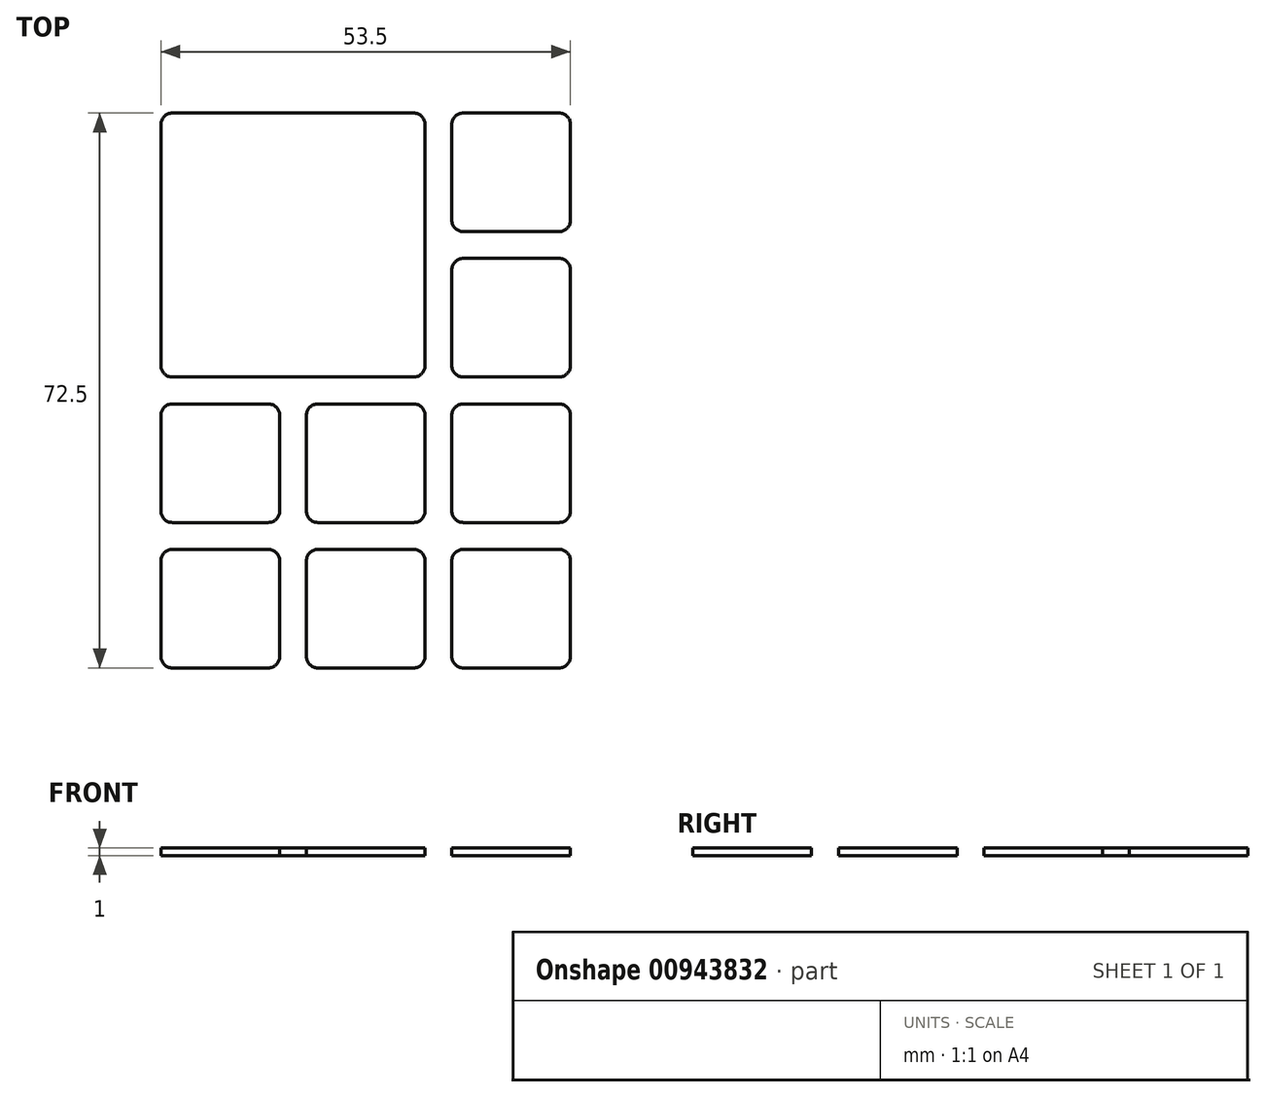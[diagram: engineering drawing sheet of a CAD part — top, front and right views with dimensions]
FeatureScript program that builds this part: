
annotation { "Feature Type Name" : "Feature", "Feature Type Description" : "" }
export const myFeature = defineFeature(function(context is Context, id is Id, definition is map)
    precondition{}
    {
        {
            var Q0;
            Q0=qCreatedBy(makeId("Top.planeOp"),FACE);
            var sketch = newSketch(context, id + "F0", { "sketchPlane" : qUnion([Q0])});
            skLineSegment(sketch, "E0.bottom", {"start": v(0, 0) * mm, "end": v(19, 0) * mm, "construction": true});
            skLineSegment(sketch, "E0.top", {"start": v(0, 19) * mm, "end": v(19, 19) * mm, "construction": true});
            skLineSegment(sketch, "E0.left", {"start": v(0, 0) * mm, "end": v(0, 19) * mm, "construction": true});
            skLineSegment(sketch, "E0.right", {"start": v(19, 0) * mm, "end": v(19, 19) * mm, "construction": true});
            skLineSegment(sketch, "E1.bottom", {"start": v(3.25, 17.25) * mm, "end": v(15.75, 17.25) * mm});
            skLineSegment(sketch, "E1.top", {"start": v(3.25, 1.75) * mm, "end": v(15.75, 1.75) * mm});
            skLineSegment(sketch, "E1.left", {"start": v(1.75, 15.75) * mm, "end": v(1.75, 3.25) * mm});
            skLineSegment(sketch, "E1.right", {"start": v(17.25, 15.75) * mm, "end": v(17.25, 3.25) * mm});
            skPoint(sketch, "E2.visualSharp", {"position": v(1.75, 17.25) * mm});
            skArc(sketch, "E2.filletArc", {"start": v(3.25, 17.25) * mm, "mid": v(2.19, 16.81) * mm, "end": v(1.75, 15.75) * mm});
            skPoint(sketch, "E3.visualSharp", {"position": v(17.25, 17.25) * mm});
            skArc(sketch, "E3.filletArc", {"start": v(17.25, 15.75) * mm, "mid": v(16.81, 16.81) * mm, "end": v(15.75, 17.25) * mm});
            skPoint(sketch, "E4.visualSharp", {"position": v(17.25, 1.75) * mm});
            skArc(sketch, "E4.filletArc", {"start": v(15.75, 1.75) * mm, "mid": v(16.81, 2.19) * mm, "end": v(17.25, 3.25) * mm});
            skPoint(sketch, "E5.visualSharp", {"position": v(1.75, 1.75) * mm});
            skArc(sketch, "E5.filletArc", {"start": v(1.75, 3.25) * mm, "mid": v(2.19, 2.19) * mm, "end": v(3.25, 1.75) * mm});
            skArc(sketch, "E6.0.1.0", {"start": v(17.25, 34.75) * mm, "mid": v(16.81, 35.81) * mm, "end": v(15.75, 36.25) * mm});
            skPoint(sketch, "E6.0.1.1", {"position": v(17.25, 36.25) * mm});
            skArc(sketch, "E6.0.1.2", {"start": v(15.75, 20.75) * mm, "mid": v(16.81, 21.19) * mm, "end": v(17.25, 22.25) * mm});
            skLineSegment(sketch, "E6.0.1.3", {"start": v(3.25, 36.25) * mm, "end": v(15.75, 36.25) * mm});
            skLineSegment(sketch, "E6.0.1.4", {"start": v(17.25, 34.75) * mm, "end": v(17.25, 22.25) * mm});
            skPoint(sketch, "E6.0.1.5", {"position": v(1.75, 20.75) * mm});
            skArc(sketch, "E6.0.1.6", {"start": v(3.25, 36.25) * mm, "mid": v(2.19, 35.81) * mm, "end": v(1.75, 34.75) * mm});
            skPoint(sketch, "E6.0.1.7", {"position": v(17.25, 20.75) * mm});
            skArc(sketch, "E6.0.1.8", {"start": v(1.75, 22.25) * mm, "mid": v(2.19, 21.19) * mm, "end": v(3.25, 20.75) * mm});
            skLineSegment(sketch, "E6.0.1.9", {"start": v(1.75, 34.75) * mm, "end": v(1.75, 22.25) * mm});
            skLineSegment(sketch, "E6.0.1.10", {"start": v(3.25, 20.75) * mm, "end": v(15.75, 20.75) * mm});
            skPoint(sketch, "E6.0.1.11", {"position": v(1.75, 36.25) * mm});
            skPoint(sketch, "E6.0.2.5", {"position": v(1.75, 39.75) * mm});
            skArc(sketch, "E6.0.2.8", {"start": v(1.75, 41.25) * mm, "mid": v(2.19, 40.19) * mm, "end": v(3.25, 39.75) * mm});
            skLineSegment(sketch, "E6.0.2.9", {"start": v(1.75, 53.75) * mm, "end": v(1.75, 41.25) * mm});
            skLineSegment(sketch, "E6.0.2.10", {"start": v(3.25, 39.75) * mm, "end": v(15.75, 39.75) * mm});
            skPoint(sketch, "E6.0.2.11", {"position": v(1.75, 55.25) * mm});
            skLineSegment(sketch, "E6.0.3.3", {"start": v(3.25, 74.25) * mm, "end": v(15.75, 74.25) * mm});
            skPoint(sketch, "E6.0.3.5", {"position": v(1.75, 58.75) * mm});
            skArc(sketch, "E6.0.3.6", {"start": v(3.25, 74.25) * mm, "mid": v(2.19, 73.81) * mm, "end": v(1.75, 72.75) * mm});
            skLineSegment(sketch, "E6.0.3.9", {"start": v(1.75, 72.75) * mm, "end": v(1.75, 60.25) * mm});
            skPoint(sketch, "E6.0.3.11", {"position": v(1.75, 74.25) * mm});
            skArc(sketch, "E6.1.0.0", {"start": v(36.25, 15.75) * mm, "mid": v(35.81, 16.81) * mm, "end": v(34.75, 17.25) * mm});
            skPoint(sketch, "E6.1.0.1", {"position": v(36.25, 17.25) * mm});
            skArc(sketch, "E6.1.0.2", {"start": v(34.75, 1.75) * mm, "mid": v(35.81, 2.19) * mm, "end": v(36.25, 3.25) * mm});
            skLineSegment(sketch, "E6.1.0.3", {"start": v(22.25, 17.25) * mm, "end": v(34.75, 17.25) * mm});
            skLineSegment(sketch, "E6.1.0.4", {"start": v(36.25, 15.75) * mm, "end": v(36.25, 3.25) * mm});
            skPoint(sketch, "E6.1.0.5", {"position": v(20.75, 1.75) * mm});
            skArc(sketch, "E6.1.0.6", {"start": v(22.25, 17.25) * mm, "mid": v(21.19, 16.81) * mm, "end": v(20.75, 15.75) * mm});
            skPoint(sketch, "E6.1.0.7", {"position": v(36.25, 1.75) * mm});
            skArc(sketch, "E6.1.0.8", {"start": v(20.75, 3.25) * mm, "mid": v(21.19, 2.19) * mm, "end": v(22.25, 1.75) * mm});
            skLineSegment(sketch, "E6.1.0.9", {"start": v(20.75, 15.75) * mm, "end": v(20.75, 3.25) * mm});
            skLineSegment(sketch, "E6.1.0.10", {"start": v(22.25, 1.75) * mm, "end": v(34.75, 1.75) * mm});
            skPoint(sketch, "E6.1.0.11", {"position": v(20.75, 17.25) * mm});
            skArc(sketch, "E6.1.1.0", {"start": v(36.25, 34.75) * mm, "mid": v(35.81, 35.81) * mm, "end": v(34.75, 36.25) * mm});
            skPoint(sketch, "E6.1.1.1", {"position": v(36.25, 36.25) * mm});
            skArc(sketch, "E6.1.1.2", {"start": v(34.75, 20.75) * mm, "mid": v(35.81, 21.19) * mm, "end": v(36.25, 22.25) * mm});
            skLineSegment(sketch, "E6.1.1.3", {"start": v(22.25, 36.25) * mm, "end": v(34.75, 36.25) * mm});
            skLineSegment(sketch, "E6.1.1.4", {"start": v(36.25, 34.75) * mm, "end": v(36.25, 22.25) * mm});
            skPoint(sketch, "E6.1.1.5", {"position": v(20.75, 20.75) * mm});
            skArc(sketch, "E6.1.1.6", {"start": v(22.25, 36.25) * mm, "mid": v(21.19, 35.81) * mm, "end": v(20.75, 34.75) * mm});
            skPoint(sketch, "E6.1.1.7", {"position": v(36.25, 20.75) * mm});
            skArc(sketch, "E6.1.1.8", {"start": v(20.75, 22.25) * mm, "mid": v(21.19, 21.19) * mm, "end": v(22.25, 20.75) * mm});
            skLineSegment(sketch, "E6.1.1.9", {"start": v(20.75, 34.75) * mm, "end": v(20.75, 22.25) * mm});
            skLineSegment(sketch, "E6.1.1.10", {"start": v(22.25, 20.75) * mm, "end": v(34.75, 20.75) * mm});
            skPoint(sketch, "E6.1.1.11", {"position": v(20.75, 36.25) * mm});
            skArc(sketch, "E6.1.2.2", {"start": v(34.75, 39.75) * mm, "mid": v(35.81, 40.19) * mm, "end": v(36.25, 41.25) * mm});
            skLineSegment(sketch, "E6.1.2.4", {"start": v(36.25, 53.75) * mm, "end": v(36.25, 41.25) * mm});
            skPoint(sketch, "E6.1.2.7", {"position": v(36.25, 39.75) * mm});
            skLineSegment(sketch, "E6.1.2.10", {"start": v(22.25, 39.75) * mm, "end": v(34.75, 39.75) * mm});
            skArc(sketch, "E6.1.3.0", {"start": v(36.25, 72.75) * mm, "mid": v(35.81, 73.81) * mm, "end": v(34.75, 74.25) * mm});
            skPoint(sketch, "E6.1.3.1", {"position": v(36.25, 74.25) * mm});
            skLineSegment(sketch, "E6.1.3.3", {"start": v(22.25, 74.25) * mm, "end": v(34.75, 74.25) * mm});
            skLineSegment(sketch, "E6.1.3.4", {"start": v(36.25, 72.75) * mm, "end": v(36.25, 60.25) * mm});
            skArc(sketch, "E6.2.0.0", {"start": v(55.25, 15.75) * mm, "mid": v(54.81, 16.81) * mm, "end": v(53.75, 17.25) * mm});
            skPoint(sketch, "E6.2.0.1", {"position": v(55.25, 17.25) * mm});
            skArc(sketch, "E6.2.0.2", {"start": v(53.75, 1.75) * mm, "mid": v(54.81, 2.19) * mm, "end": v(55.25, 3.25) * mm});
            skLineSegment(sketch, "E6.2.0.3", {"start": v(41.25, 17.25) * mm, "end": v(53.75, 17.25) * mm});
            skLineSegment(sketch, "E6.2.0.4", {"start": v(55.25, 15.75) * mm, "end": v(55.25, 3.25) * mm});
            skPoint(sketch, "E6.2.0.5", {"position": v(39.75, 1.75) * mm});
            skArc(sketch, "E6.2.0.6", {"start": v(41.25, 17.25) * mm, "mid": v(40.19, 16.81) * mm, "end": v(39.75, 15.75) * mm});
            skPoint(sketch, "E6.2.0.7", {"position": v(55.25, 1.75) * mm});
            skArc(sketch, "E6.2.0.8", {"start": v(39.75, 3.25) * mm, "mid": v(40.19, 2.19) * mm, "end": v(41.25, 1.75) * mm});
            skLineSegment(sketch, "E6.2.0.9", {"start": v(39.75, 15.75) * mm, "end": v(39.75, 3.25) * mm});
            skLineSegment(sketch, "E6.2.0.10", {"start": v(41.25, 1.75) * mm, "end": v(53.75, 1.75) * mm});
            skPoint(sketch, "E6.2.0.11", {"position": v(39.75, 17.25) * mm});
            skArc(sketch, "E6.2.1.0", {"start": v(55.25, 34.75) * mm, "mid": v(54.81, 35.81) * mm, "end": v(53.75, 36.25) * mm});
            skPoint(sketch, "E6.2.1.1", {"position": v(55.25, 36.25) * mm});
            skArc(sketch, "E6.2.1.2", {"start": v(53.75, 20.75) * mm, "mid": v(54.81, 21.19) * mm, "end": v(55.25, 22.25) * mm});
            skLineSegment(sketch, "E6.2.1.3", {"start": v(41.25, 36.25) * mm, "end": v(53.75, 36.25) * mm});
            skLineSegment(sketch, "E6.2.1.4", {"start": v(55.25, 34.75) * mm, "end": v(55.25, 22.25) * mm});
            skPoint(sketch, "E6.2.1.5", {"position": v(39.75, 20.75) * mm});
            skArc(sketch, "E6.2.1.6", {"start": v(41.25, 36.25) * mm, "mid": v(40.19, 35.81) * mm, "end": v(39.75, 34.75) * mm});
            skPoint(sketch, "E6.2.1.7", {"position": v(55.25, 20.75) * mm});
            skArc(sketch, "E6.2.1.8", {"start": v(39.75, 22.25) * mm, "mid": v(40.19, 21.19) * mm, "end": v(41.25, 20.75) * mm});
            skLineSegment(sketch, "E6.2.1.9", {"start": v(39.75, 34.75) * mm, "end": v(39.75, 22.25) * mm});
            skLineSegment(sketch, "E6.2.1.10", {"start": v(41.25, 20.75) * mm, "end": v(53.75, 20.75) * mm});
            skPoint(sketch, "E6.2.1.11", {"position": v(39.75, 36.25) * mm});
            skArc(sketch, "E6.2.2.0", {"start": v(55.25, 53.75) * mm, "mid": v(54.81, 54.81) * mm, "end": v(53.75, 55.25) * mm});
            skPoint(sketch, "E6.2.2.1", {"position": v(55.25, 55.25) * mm});
            skArc(sketch, "E6.2.2.2", {"start": v(53.75, 39.75) * mm, "mid": v(54.81, 40.19) * mm, "end": v(55.25, 41.25) * mm});
            skLineSegment(sketch, "E6.2.2.3", {"start": v(41.25, 55.25) * mm, "end": v(53.75, 55.25) * mm});
            skLineSegment(sketch, "E6.2.2.4", {"start": v(55.25, 53.75) * mm, "end": v(55.25, 41.25) * mm});
            skPoint(sketch, "E6.2.2.5", {"position": v(39.75, 39.75) * mm});
            skArc(sketch, "E6.2.2.6", {"start": v(41.25, 55.25) * mm, "mid": v(40.19, 54.81) * mm, "end": v(39.75, 53.75) * mm});
            skPoint(sketch, "E6.2.2.7", {"position": v(55.25, 39.75) * mm});
            skArc(sketch, "E6.2.2.8", {"start": v(39.75, 41.25) * mm, "mid": v(40.19, 40.19) * mm, "end": v(41.25, 39.75) * mm});
            skLineSegment(sketch, "E6.2.2.9", {"start": v(39.75, 53.75) * mm, "end": v(39.75, 41.25) * mm});
            skLineSegment(sketch, "E6.2.2.10", {"start": v(41.25, 39.75) * mm, "end": v(53.75, 39.75) * mm});
            skPoint(sketch, "E6.2.2.11", {"position": v(39.75, 55.25) * mm});
            skArc(sketch, "E6.2.3.0", {"start": v(55.25, 72.75) * mm, "mid": v(54.81, 73.81) * mm, "end": v(53.75, 74.25) * mm});
            skPoint(sketch, "E6.2.3.1", {"position": v(55.25, 74.25) * mm});
            skArc(sketch, "E6.2.3.2", {"start": v(53.75, 58.75) * mm, "mid": v(54.81, 59.19) * mm, "end": v(55.25, 60.25) * mm});
            skLineSegment(sketch, "E6.2.3.3", {"start": v(41.25, 74.25) * mm, "end": v(53.75, 74.25) * mm});
            skLineSegment(sketch, "E6.2.3.4", {"start": v(55.25, 72.75) * mm, "end": v(55.25, 60.25) * mm});
            skPoint(sketch, "E6.2.3.5", {"position": v(39.75, 58.75) * mm});
            skArc(sketch, "E6.2.3.6", {"start": v(41.25, 74.25) * mm, "mid": v(40.19, 73.81) * mm, "end": v(39.75, 72.75) * mm});
            skPoint(sketch, "E6.2.3.7", {"position": v(55.25, 58.75) * mm});
            skArc(sketch, "E6.2.3.8", {"start": v(39.75, 60.25) * mm, "mid": v(40.19, 59.19) * mm, "end": v(41.25, 58.75) * mm});
            skLineSegment(sketch, "E6.2.3.9", {"start": v(39.75, 72.75) * mm, "end": v(39.75, 60.25) * mm});
            skLineSegment(sketch, "E6.2.3.10", {"start": v(41.25, 58.75) * mm, "end": v(53.75, 58.75) * mm});
            skPoint(sketch, "E6.2.3.11", {"position": v(39.75, 74.25) * mm});
            skLineSegment(sketch, "E6.direction1", {"start": v(1.75, 1.75) * mm, "end": v(20.75, 1.75) * mm, "construction": true});
            skLineSegment(sketch, "E6.direction2", {"start": v(1.75, 1.75) * mm, "end": v(1.75, 20.75) * mm, "construction": true});
            skLineSegment(sketch, "E7", {"start": v(1.75, 53.75) * mm, "end": v(1.75, 60.25) * mm});
            skLineSegment(sketch, "E8", {"start": v(36.25, 53.75) * mm, "end": v(36.25, 60.25) * mm});
            skLineSegment(sketch, "E9", {"start": v(15.75, 74.25) * mm, "end": v(22.25, 74.25) * mm});
            skLineSegment(sketch, "E10", {"start": v(15.75, 39.75) * mm, "end": v(22.25, 39.75) * mm});
            skSolve(sketch);
        }
        {
            var Q0;
            Q0=qSketchRegion(id+"F0",true);
            extrude(context, id + "F1", {"entities" : qUnion([Q0]), "depth" : 1 * mm, "offsetDistance" : 25 * mm});
        }
    });
